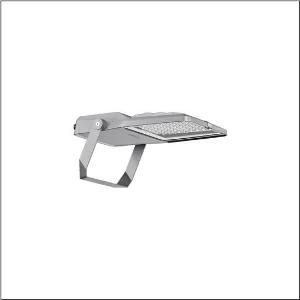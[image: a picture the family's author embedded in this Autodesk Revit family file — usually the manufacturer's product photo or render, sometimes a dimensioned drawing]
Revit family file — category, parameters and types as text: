
# Revit family: floodlight_fl_21_iq_mini___pl43_5xa7772b3a1a_8813
name_source: partatom
category: Lighting Fixtures
units: mm (PartAtom-declared; Revit-internal decimal feet)

## family parameters
Cut with Voids When Loaded = No
Host = Face
Light Source = No
Part Type = Normal
Room Calculation Point = No
Round Connector Dimension = Use Diameter
Shared = No

## types (1)
- --- (1 x LED, 5510 lm, 45.5 W, 3000K)
    Apparent Load = 46 VA
    CIE Flux Codes = 27 78 99 100 100
    Color Rendering = 80
    Color Temperature = 3000K
    Default Elevation = 1800 mm
    Description = Floodlight FL 21 iQ mini, floodlight, primary light control with lens, of PMMA, primary optical cover: protective disc, of toughened safety glass, transparent, light distribution: PL43, light emission: direct distribution, installation type: surface-mounted, LED, High Power LED, rated luminous flux: 5.510lm, luminous efficacy: 121lm/W, light colour: 830, colour temperature: 3000K, control: Street-Remote, Auto-Match, Temp-Guard, Night-Set, Smart-Wire, Desk-Remote (wireless, voltage-free reading and setting of iQ features in the workshop via application-optimized NFC function/RFID function), optimised constant luminous flux control (CLO 2.0), with terminal, 6-pole, mains connection: 220..240V, AC, 50/60Hz, start of lifetime: 46W, end of service life: 48W, reduction: 21W, luminaire housing, of diecast aluminium, powder-coated, Siteco® metallic grey (DB 702S), corrosivity category C5 mid according to DIN EN ISO 12944, sealing non-destructively replaceable, mounting bracket, of steel, galvanised, powder-coated, Siteco® metallic grey (DB 702S), protection rating (complete): IP66, insulation class (complete): insulation class II (safety insulation), certification: CE, ENEC, VDE, protection symbol: D, impact resistance: IK08, permissible operating ambient temperature: -40..+40°C, permissible operating ambient temperature for outdoor applications: -40..+50°C, standard: DIN EN 12944, LABS conformity tested according to VDMA 24364:2018-05, packaging unit: 1 piece

Light Distribution: PL43
    Height = 70 mm
    Lamp = 1 x LED
    Lamp Light Flux = 5510 lm
    Lamp Power = 45.5 W
    Lamp count = 1
    Length = 485 mm
    Luminous efficacy = 121 lm/W
    Manufacturer = Siteco
    ModVariant = No
    Model = 5XA7772B3A1A
    Number of Poles = 1
    OnlyDefault = Yes
    Power Factor = 1
    Product Name = Floodlight FL 21 iQ mini | PL43
    Product group = floodlight | pylon annexe
    ProductGroupID = 6200
    Protection Class = Protection class II
    Protection Degree = IP 66
    RLX_Detail_Level = 1
    RLX_Emergency_Light_Flux = 0 lm
    RLX_Emergency_Type = 0
    RLX_Emergency_Type_DB = No
    RlxData = <blob elided: 96173 chars, md5=5bfd23df>
    Socket = socket
    Standby Power = 0 W
    System Light Flux = 5510 lm
    System Power = 46 W
    Type Comments = factory setting: luminous flux: 100 % | dim-lin: 254 | 463 mA
    Type Image = l_1006845.jpg
    URL = http://relux.com
    VarID = @adj_112905
    Voltage = 0 V
    Weight = 0.00 kg
    Width = 337 mm

## geometry (parser evidence)
native form markers: Blend x4, Sweep x13
no freeform markers — native parametric forms only
